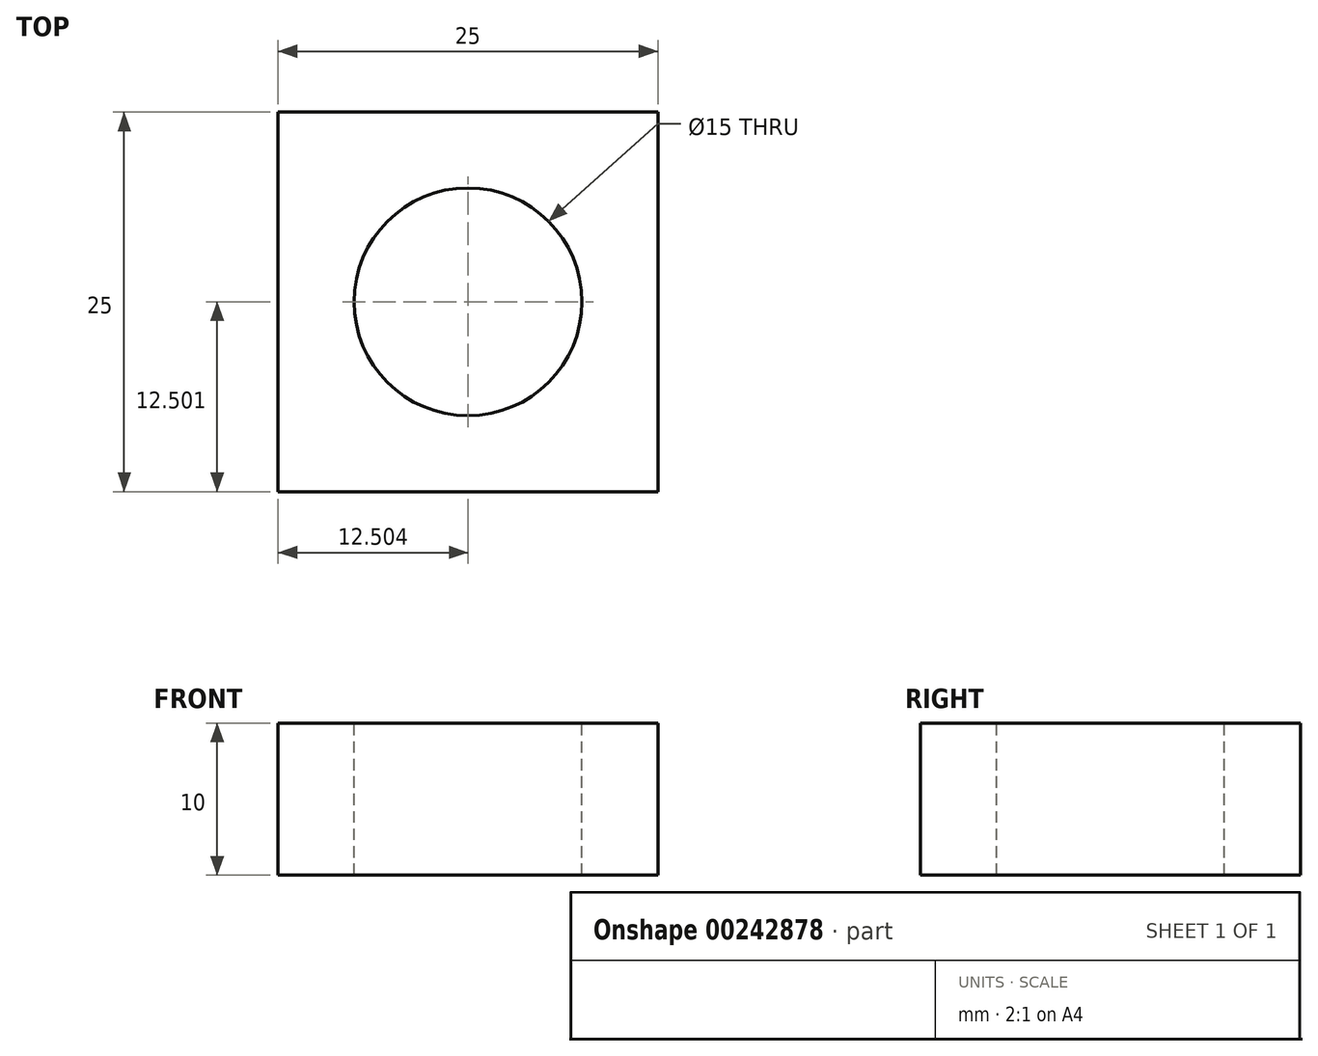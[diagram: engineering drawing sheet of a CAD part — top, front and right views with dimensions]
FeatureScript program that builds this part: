
annotation { "Feature Type Name" : "Feature", "Feature Type Description" : "" }
export const myFeature = defineFeature(function(context is Context, id is Id, definition is map)
    precondition{}
    {
        {
            var Q0;
            Q0=qCreatedBy(makeId("Top.planeOp"),FACE);
            var sketch = newSketch(context, id + "F0", { "sketchPlane" : qUnion([Q0])});
            skLineSegment(sketch, "E0.bottom", {"start": v(-27.4, 23.72) * mm, "end": v(-2.4, 23.72) * mm});
            skLineSegment(sketch, "E0.top", {"start": v(-27.4, -1.28) * mm, "end": v(-2.4, -1.28) * mm});
            skLineSegment(sketch, "E0.left", {"start": v(-27.4, 23.72) * mm, "end": v(-27.4, -1.28) * mm});
            skLineSegment(sketch, "E0.right", {"start": v(-2.4, 23.72) * mm, "end": v(-2.4, -1.28) * mm});
            skSolve(sketch);
        }
        {
            var Q0;
            Q0 = qSketchRegion(id + "F0", true);
            extrude(context, id + "F1", {"entities" : qUnion([Q0]), "depth" : 10 * mm});
        }
        {
            var Q0;
            Q0=makeQuery(id+"F1.opExtrude","CAP_FACE",FACE,{"disambiguationData":[OSD([sQuery(id+"F0.wireOp",EDGE,"E0.bottom"),sQuery(id+"F0.wireOp",EDGE,"E0.top"),sQuery(id+"F0.wireOp",EDGE,"E0.left"),sQuery(id+"F0.wireOp",EDGE,"E0.right")])],"isStart":false});
            var sketch = newSketch(context, id + "F2", { "sketchPlane" : qUnion([Q0])});
            skCircle(sketch, "E1", {"center": v(-14.9, 11.22) * mm, "radius": 7.5 * mm});
            skPoint(sketch, "E1.centerSnap0", {"position": v(-27.4, 11.22) * mm});
            skPoint(sketch, "E1.centerSnap1", {"position": v(-14.9, 23.72) * mm});
            skSolve(sketch);
        }
        {
            var Q0;
            Q0 = qSketchRegion(id + "F2", true);
            extrude(context, id + "F3", {"entities" : qUnion([Q0]), "operationType" : NewBodyOperationType.REMOVE, "endBound" : BoundingType.THROUGH_ALL, "oppositeDirection" : true, "depth" : 25 * mm});
        }
    });
